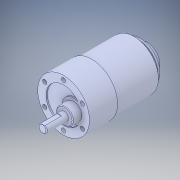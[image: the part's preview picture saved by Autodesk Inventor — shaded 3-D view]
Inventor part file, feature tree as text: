
AUTODESK INVENTOR PART (.ipt)
format: ipt  version: 2017 (Build 210142000, 142)  size: 188,928 bytes
history: native  units: in
note: dims shown in document units (in); Inventor stores cm internally (conversion verified against a paired STEP export)
features: other x2, fillet x1
ambient origin geometry x8: Origin, YZ Plane, XZ Plane, XY Plane, X Axis, Y Axis, Z Axis, Center Point
bodies: Solid1 (feature_tree), Solid2 (feature_tree), Solid3 (feature_tree)
feature tree (3):
  other  "Boss-Extrude6"
  other  "Boss-Extrude8"
  fillet  "Fillet4"  [1 undecoded]
note: 1 required parameter value undecoded (feature->parameter linkage not recoverable at this tier; creation-order binding heuristic only, values carry confidence <= 0.55)
